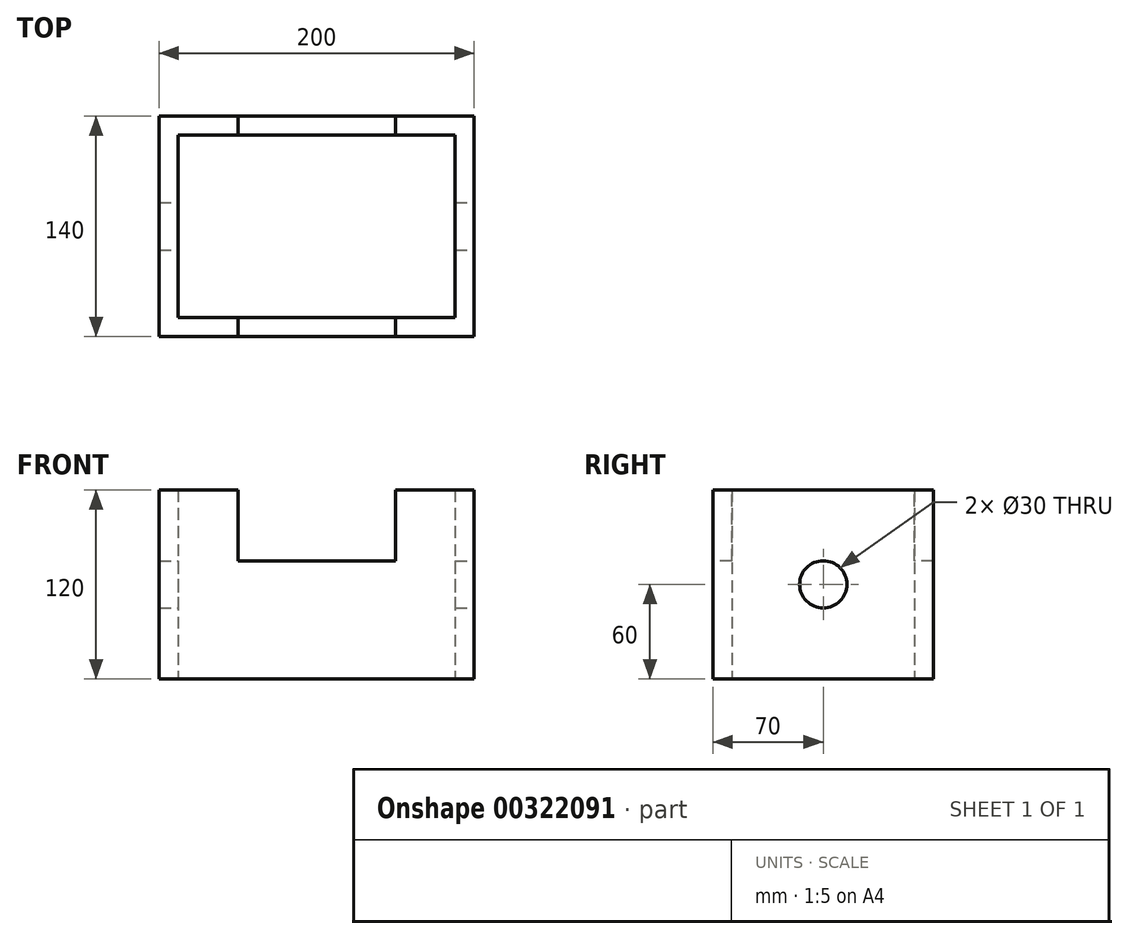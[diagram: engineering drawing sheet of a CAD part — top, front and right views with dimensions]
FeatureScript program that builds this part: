
annotation { "Feature Type Name" : "Feature", "Feature Type Description" : "" }
export const myFeature = defineFeature(function(context is Context, id is Id, definition is map)
    precondition{}
    {
        {
            var Q0;
            Q0=qCreatedBy(makeId("Top.planeOp"),FACE);
            var sketch = newSketch(context, id + "F0", { "sketchPlane" : qUnion([Q0])});
            skLineSegment(sketch, "E0.bottom", {"start": v(100, -70) * mm, "end": v(-100, -70) * mm});
            skLineSegment(sketch, "E0.top", {"start": v(100, 70) * mm, "end": v(-100, 70) * mm});
            skLineSegment(sketch, "E0.left", {"start": v(100, -70) * mm, "end": v(100, 70) * mm});
            skLineSegment(sketch, "E0.right", {"start": v(-100, -70) * mm, "end": v(-100, 70) * mm});
            skPoint(sketch, "E0.middle", {"position": v(0, 0) * mm});
            skLineSegment(sketch, "E1.bottom", {"start": v(88, -58) * mm, "end": v(-88, -58) * mm});
            skLineSegment(sketch, "E1.top", {"start": v(88, 58) * mm, "end": v(-88, 58) * mm});
            skLineSegment(sketch, "E1.left", {"start": v(88, -58) * mm, "end": v(88, 58) * mm});
            skLineSegment(sketch, "E1.right", {"start": v(-88, -58) * mm, "end": v(-88, 58) * mm});
            skSolve(sketch);
        }
        {
            var Q0;
            Q0=makeQuery(id+"F0.imprint","IMPRINT",FACE,{"disambiguationData":[TD([[makeQuery(id+"F0.imprint","IMPRINT",EDGE,{"derivedFrom":sQuery(id+"F0.wireOp",EDGE,"E0.bottom")}),-1.0]])]});
            extrude(context, id + "F1", {"entities" : qUnion([Q0]), "depth" : 120 * mm});
        }
        {
            var Q0;
            Q0=makeQuery(id+"F1.opExtrude","SWEPT_FACE",FACE,{"disambiguationData":[OSD([sQuery(id+"F0.wireOp",EDGE,"E0.left")])]});
            var sketch = newSketch(context, id + "F2", { "sketchPlane" : qUnion([Q0])});
            skLineSegment(sketch, "E2", {"start": v(-70, 120) * mm, "end": v(70, 0) * mm, "construction": true});
            skLineSegment(sketch, "E3", {"start": v(70, 0) * mm, "end": v(-70, 0) * mm, "construction": true});
            skLineSegment(sketch, "E4", {"start": v(-70, 0) * mm, "end": v(70, 120) * mm, "construction": true});
            skCircle(sketch, "E5", {"center": v(0, 60) * mm, "radius": 15 * mm});
            skSolve(sketch);
        }
        {
            var Q0;
            Q0=makeQuery(id+"F2.imprint","IMPRINT",FACE,{"disambiguationData":[TD([[makeQuery(id+"F2.imprint","IMPRINT",EDGE,{"derivedFrom":sQuery(id+"F2.wireOp",EDGE,"E5")}),1.0]])]});
            extrude(context, id + "F3", {"entities" : qUnion([Q0]), "operationType" : NewBodyOperationType.REMOVE, "endBound" : BoundingType.THROUGH_ALL, "oppositeDirection" : true, "depth" : 25 * mm});
        }
        {
            var Q0;
            Q0=makeQuery(id+"F1.opExtrude","SWEPT_FACE",FACE,{"disambiguationData":[OSD([sQuery(id+"F0.wireOp",EDGE,"E0.bottom")])]});
            var sketch = newSketch(context, id + "F4", { "sketchPlane" : qUnion([Q0])});
            skLineSegment(sketch, "E6", {"start": v(0, 0) * mm, "end": v(0, 120) * mm, "construction": true});
            skLineSegment(sketch, "E7.bottom", {"start": v(50, 75) * mm, "end": v(-50, 75) * mm});
            skLineSegment(sketch, "E7.top", {"start": v(50, 120) * mm, "end": v(-50, 120) * mm});
            skLineSegment(sketch, "E7.left", {"start": v(50, 75) * mm, "end": v(50, 120) * mm});
            skLineSegment(sketch, "E7.right", {"start": v(-50, 75) * mm, "end": v(-50, 120) * mm});
            skPoint(sketch, "E7.middle", {"position": v(0, 97.5) * mm});
            skSolve(sketch);
        }
        {
            var Q0;
            Q0=makeQuery(id+"F4.imprint","IMPRINT",FACE,{"disambiguationData":[TD([[makeQuery(id+"F4.imprint","IMPRINT",EDGE,{"derivedFrom":sQuery(id+"F4.wireOp",EDGE,"E7.bottom")}),-1.0]])]});
            extrude(context, id + "F5", {"entities" : qUnion([Q0]), "operationType" : NewBodyOperationType.REMOVE, "endBound" : BoundingType.THROUGH_ALL, "oppositeDirection" : true, "depth" : 25 * mm});
        }
    });
